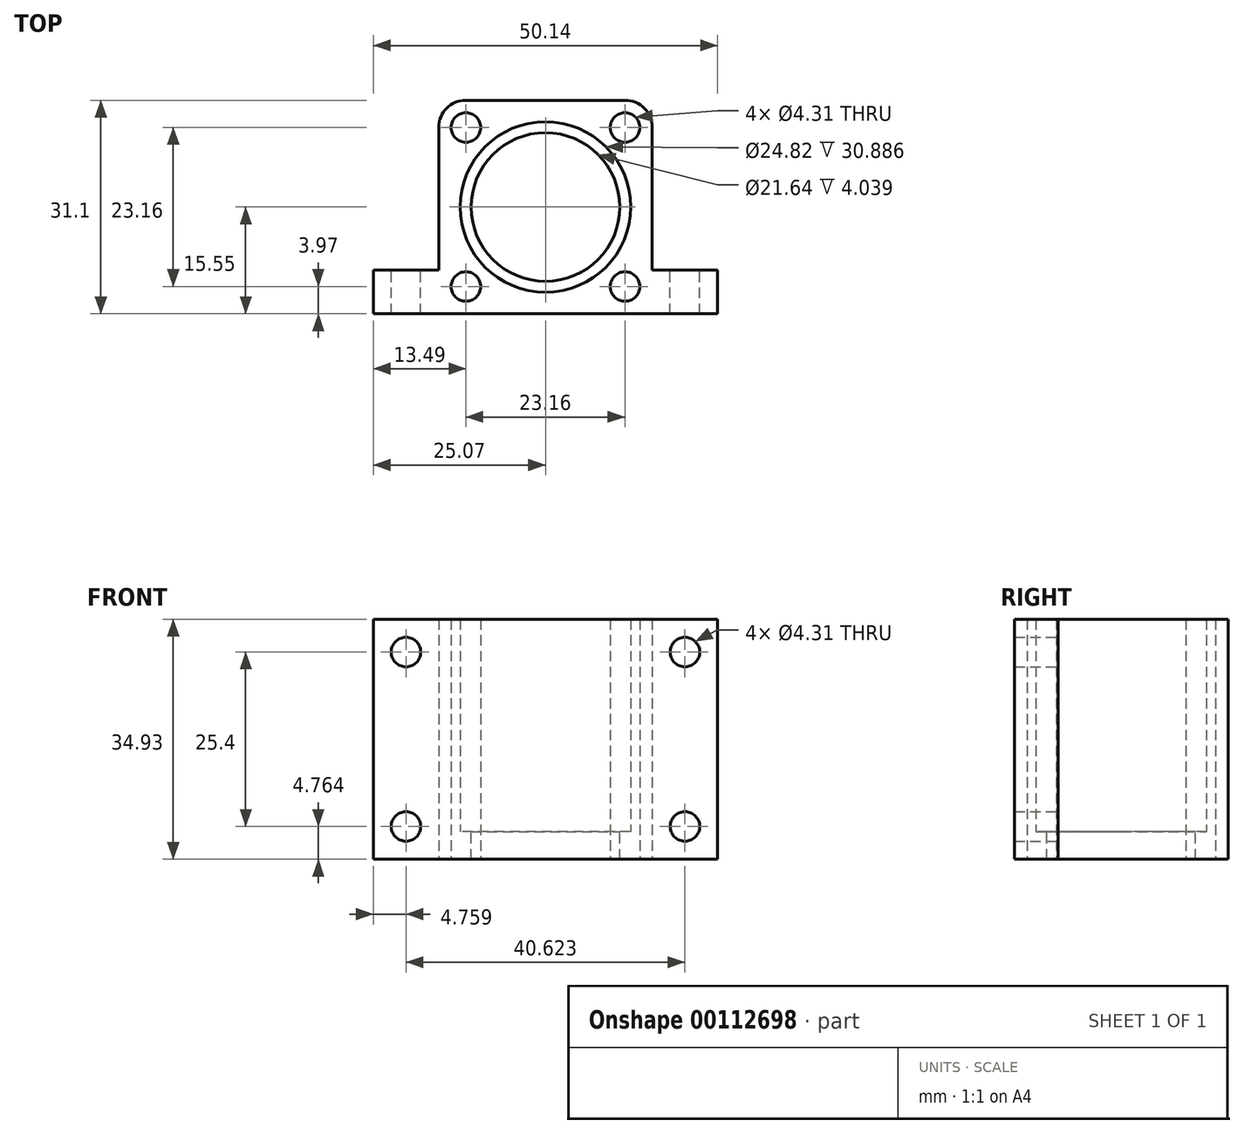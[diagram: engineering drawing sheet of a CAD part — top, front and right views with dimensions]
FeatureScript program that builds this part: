
annotation { "Feature Type Name" : "Feature", "Feature Type Description" : "" }
export const myFeature = defineFeature(function(context is Context, id is Id, definition is map)
    precondition{}
    {
        {
            var Q0;
            Q0=qCreatedBy(makeId("Top.planeOp"),FACE);
            var sketch = newSketch(context, id + "F0", { "sketchPlane" : qUnion([Q0])});
            skLineSegment(sketch, "E0.bottom", {"start": v(11.58, -11.58) * mm, "end": v(-11.58, -11.58) * mm, "construction": true});
            skLineSegment(sketch, "E0.top", {"start": v(11.58, 11.58) * mm, "end": v(-11.58, 11.58) * mm, "construction": true});
            skLineSegment(sketch, "E0.left", {"start": v(11.58, -11.58) * mm, "end": v(11.58, 11.58) * mm, "construction": true});
            skLineSegment(sketch, "E0.right", {"start": v(-11.58, -11.58) * mm, "end": v(-11.58, 11.58) * mm, "construction": true});
            skPoint(sketch, "E0.middle", {"position": v(0, 0) * mm});
            skCircle(sketch, "E1", {"center": v(0, 0) * mm, "radius": 12.4 * mm});
            skCircle(sketch, "E2", {"center": v(11.58, 11.58) * mm, "radius": 2.15 * mm});
            skCircle(sketch, "E3", {"center": v(-11.58, 11.58) * mm, "radius": 2.15 * mm});
            skCircle(sketch, "E4", {"center": v(-11.58, -11.58) * mm, "radius": 2.15 * mm});
            skCircle(sketch, "E5", {"center": v(11.58, -11.58) * mm, "radius": 2.15 * mm});
            skLineSegment(sketch, "E6.top", {"start": v(-15.55, 15.55) * mm, "end": v(15.55, 15.55) * mm});
            skLineSegment(sketch, "E6.left", {"start": v(-15.55, -9.2) * mm, "end": v(-15.55, 15.55) * mm});
            skLineSegment(sketch, "E6.right", {"start": v(15.55, -9.2) * mm, "end": v(15.55, 15.55) * mm});
            skCircle(sketch, "E7", {"center": v(-11.58, 11.58) * mm, "radius": 3.97 * mm, "construction": true});
            skLineSegment(sketch, "E8", {"start": v(0, 0) * mm, "end": v(0, 15.55) * mm, "construction": true});
            skLineSegment(sketch, "E9", {"start": v(-15.55, -9.2) * mm, "end": v(-25.07, -9.2) * mm});
            skLineSegment(sketch, "E10", {"start": v(-25.07, -9.2) * mm, "end": v(-25.07, -15.55) * mm});
            skLineSegment(sketch, "E11", {"start": v(-25.07, -15.55) * mm, "end": v(25.07, -15.55) * mm});
            skLineSegment(sketch, "E12", {"start": v(25.07, -15.55) * mm, "end": v(25.07, -9.2) * mm});
            skLineSegment(sketch, "E13", {"start": v(25.07, -9.2) * mm, "end": v(15.55, -9.2) * mm});
            skCircle(sketch, "E14", {"center": v(-11.58, -11.58) * mm, "radius": 3.97 * mm, "construction": true});
            skSolve(sketch);
        }
        {
            var Q0;
            Q0 = qSketchRegion(id + "F0", true);
            extrude(context, id + "F1", {"entities" : qUnion([Q0]), "depth" : 30.9 * mm});
        }
        {
            var Q0;
            Q0=makeQuery(id+"F1.opExtrude","CAP_FACE",FACE,{"disambiguationData":[OSD([sQuery(id+"F0.wireOp",EDGE,"E1"),sQuery(id+"F0.wireOp",EDGE,"E2"),sQuery(id+"F0.wireOp",EDGE,"E3"),sQuery(id+"F0.wireOp",EDGE,"E4"),sQuery(id+"F0.wireOp",EDGE,"E5"),sQuery(id+"F0.wireOp",EDGE,"E6.top"),sQuery(id+"F0.wireOp",EDGE,"E6.left"),sQuery(id+"F0.wireOp",EDGE,"E6.right"),sQuery(id+"F0.wireOp",EDGE,"E9"),sQuery(id+"F0.wireOp",EDGE,"E10"),sQuery(id+"F0.wireOp",EDGE,"E11"),sQuery(id+"F0.wireOp",EDGE,"E12"),sQuery(id+"F0.wireOp",EDGE,"E13")])],"isStart":true});
            var sketch = newSketch(context, id + "F2", { "sketchPlane" : qUnion([Q0])});
            skCircle(sketch, "E15", {"center": v(0, 0) * mm, "radius": 10.82 * mm});
            skSolve(sketch);
        }
        {
            var Q0;
            Q0=makeQuery(id+"F2.imprint","IMPRINT",FACE,{"disambiguationData":[TD([[makeQuery(id+"F2.imprint","IMPRINT",EDGE,{"derivedFrom":sQuery(id+"F2.wireOp",EDGE,"E15")}),-1.0]])]});
            var Q1;
            Q1=makeQuery(id+"F2.imprint","IMPRINT",FACE,{"disambiguationData":[TD([[makeQuery(id+"F2.imprint","IMPRINT",EDGE,{"derivedFrom":makeQuery(id+"F1.opExtrude","CAP_EDGE",EDGE,{"disambiguationData":[OSD([sQuery(id+"F0.wireOp",EDGE,"E1")])],"isStart":true})}),1.0]])]});
            extrude(context, id + "F3", {"entities" : qUnion([Q0, Q1]), "operationType" : NewBodyOperationType.ADD, "depth" : 4.04 * mm});
        }
        {
            var Q0;
            {var subQ0=sQuery(id+"F0.wireOp",EDGE,"E9");Q0=makeQuery(id+"F3.boolean.opBoolean","MERGE",FACE,{"derivedFrom":[makeQuery(id+"F1.opExtrude","SWEPT_FACE",FACE,{"disambiguationData":[OSD([subQ0])]}),makeQuery(id+"F3.opExtrude","SWEPT_FACE",FACE,{"disambiguationData":[OSD([subQ0])]})]});}
            var sketch = newSketch(context, id + "F4", { "sketchPlane" : qUnion([Q0])});
            skLineSegment(sketch, "E16", {"start": v(20.31, -4.04) * mm, "end": v(20.31, 0.72) * mm, "construction": true});
            skLineSegment(sketch, "E17", {"start": v(20.31, 30.89) * mm, "end": v(20.31, 26.12) * mm, "construction": true});
            skLineSegment(sketch, "E18", {"start": v(-20.31, -4.04) * mm, "end": v(-20.31, 0.72) * mm, "construction": true});
            skLineSegment(sketch, "E19", {"start": v(-20.31, 0.72) * mm, "end": v(-25.07, 0.72) * mm, "construction": true});
            skLineSegment(sketch, "E20", {"start": v(-20.31, 30.89) * mm, "end": v(-20.31, 26.12) * mm, "construction": true});
            skCircle(sketch, "E21", {"center": v(-20.31, 0.72) * mm, "radius": 2.15 * mm});
            skCircle(sketch, "E22", {"center": v(-20.31, 26.12) * mm, "radius": 2.15 * mm});
            skCircle(sketch, "E23", {"center": v(20.31, 26.12) * mm, "radius": 2.15 * mm});
            skCircle(sketch, "E24", {"center": v(20.31, 0.72) * mm, "radius": 2.15 * mm});
            skSolve(sketch);
        }
        {
            var Q0;
            Q0 = qSketchRegion(id + "F4", true);
            var Q1;
            {var subQ0=sQuery(id+"F0.wireOp",EDGE,"E11");Q1=makeQuery(id+"F3.boolean.opBoolean","MERGE",FACE,{"derivedFrom":[makeQuery(id+"F1.opExtrude","SWEPT_FACE",FACE,{"disambiguationData":[OSD([subQ0])]}),makeQuery(id+"F3.opExtrude","SWEPT_FACE",FACE,{"disambiguationData":[OSD([subQ0])]})]});}
            extrude(context, id + "F5", {"entities" : qUnion([Q0]), "operationType" : NewBodyOperationType.REMOVE, "endBound" : BoundingType.UP_TO_SURFACE, "oppositeDirection" : true, "endBoundEntityFace" : qUnion([Q1]), "depth" : 25.4 * mm});
        }
        {
            var Q0;
            {var subQ0=sQuery(id+"F0.wireOp",EDGE,"E6.left");var subQ1=sQuery(id+"F0.wireOp",EDGE,"E6.top");Q0=makeQuery(id+"F3.boolean.opBoolean","MERGE",EDGE,{"derivedFrom":[makeQuery(id+"F1.opExtrude","SWEPT_EDGE",EDGE,{"disambiguationData":[OSD([subQ1,subQ0])]}),makeQuery(id+"F3.opExtrude","SWEPT_EDGE",EDGE,{"disambiguationData":[OSD([subQ1,subQ0])]})]});}
            var Q1;
            {var subQ0=sQuery(id+"F0.wireOp",EDGE,"E6.right");var subQ1=sQuery(id+"F0.wireOp",EDGE,"E6.top");Q1=makeQuery(id+"F3.boolean.opBoolean","MERGE",EDGE,{"derivedFrom":[makeQuery(id+"F1.opExtrude","SWEPT_EDGE",EDGE,{"disambiguationData":[OSD([subQ1,subQ0])]}),makeQuery(id+"F3.opExtrude","SWEPT_EDGE",EDGE,{"disambiguationData":[OSD([subQ1,subQ0])]})]});}
            fillet(context, id + "F6", {"entities" : qUnion([Q0, Q1]), "radius" : 3.97 * mm, "tangentPropagation" : true, "allowEdgeOverflow" : false});
        }
    });
